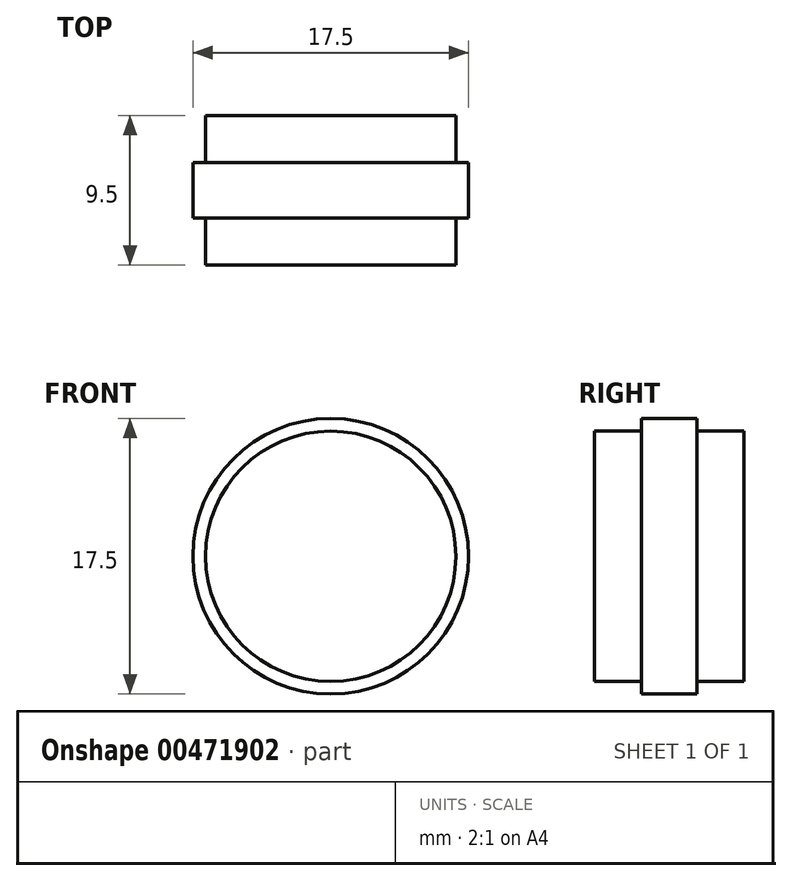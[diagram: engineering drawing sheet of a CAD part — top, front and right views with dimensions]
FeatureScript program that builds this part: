
annotation { "Feature Type Name" : "Feature", "Feature Type Description" : "" }
export const myFeature = defineFeature(function(context is Context, id is Id, definition is map)
    precondition{}
    {
        {
            var Q0;
            Q0=qCreatedBy(makeId("Front.planeOp"),FACE);
            var sketch = newSketch(context, id + "F0", { "sketchPlane" : qUnion([Q0])});
            skCircle(sketch, "E0", {"center": v(0, 0) * mm, "radius": 7.95 * mm});
            skSolve(sketch);
        }
        {
            var Q0;
            Q0=makeQuery(id+"F0.imprint","IMPRINT",FACE,{"disambiguationData":[TD([[makeQuery(id+"F0.imprint","IMPRINT",EDGE,{"derivedFrom":sQuery(id+"F0.wireOp",EDGE,"E0")}),1.0]])]});
            extrude(context, id + "F1", {"entities" : qUnion([Q0]), "depth" : 3 * mm});
        }
        {
            var Q0;
            Q0=qCreatedBy(makeId("Front.planeOp"),FACE);
            var sketch = newSketch(context, id + "F2", { "sketchPlane" : qUnion([Q0])});
            skCircle(sketch, "E1", {"center": v(0, 0) * mm, "radius": 8.75 * mm});
            skSolve(sketch);
        }
        {
            var Q0;
            Q0 = qSketchRegion(id + "F2", true);
            extrude(context, id + "F3", {"entities" : qUnion([Q0]), "operationType" : NewBodyOperationType.ADD, "oppositeDirection" : true, "depth" : 3.5 * mm});
        }
        {
            var Q0;
            Q0=makeQuery(id+"F3.opExtrude","CAP_FACE",FACE,{"disambiguationData":[OSD([sQuery(id+"F2.wireOp",EDGE,"E1")])],"isStart":false});
            var sketch = newSketch(context, id + "F4", { "sketchPlane" : qUnion([Q0])});
            skCircle(sketch, "E2", {"center": v(0, 0) * mm, "radius": 7.95 * mm});
            skSolve(sketch);
        }
        {
            var Q0;
            Q0=makeQuery(id+"F4.imprint","IMPRINT",FACE,{"disambiguationData":[TD([[makeQuery(id+"F4.imprint","IMPRINT",EDGE,{"derivedFrom":sQuery(id+"F4.wireOp",EDGE,"E2")}),1.0]])]});
            extrude(context, id + "F5", {"entities" : qUnion([Q0]), "operationType" : NewBodyOperationType.ADD, "depth" : 3 * mm});
        }
    });
